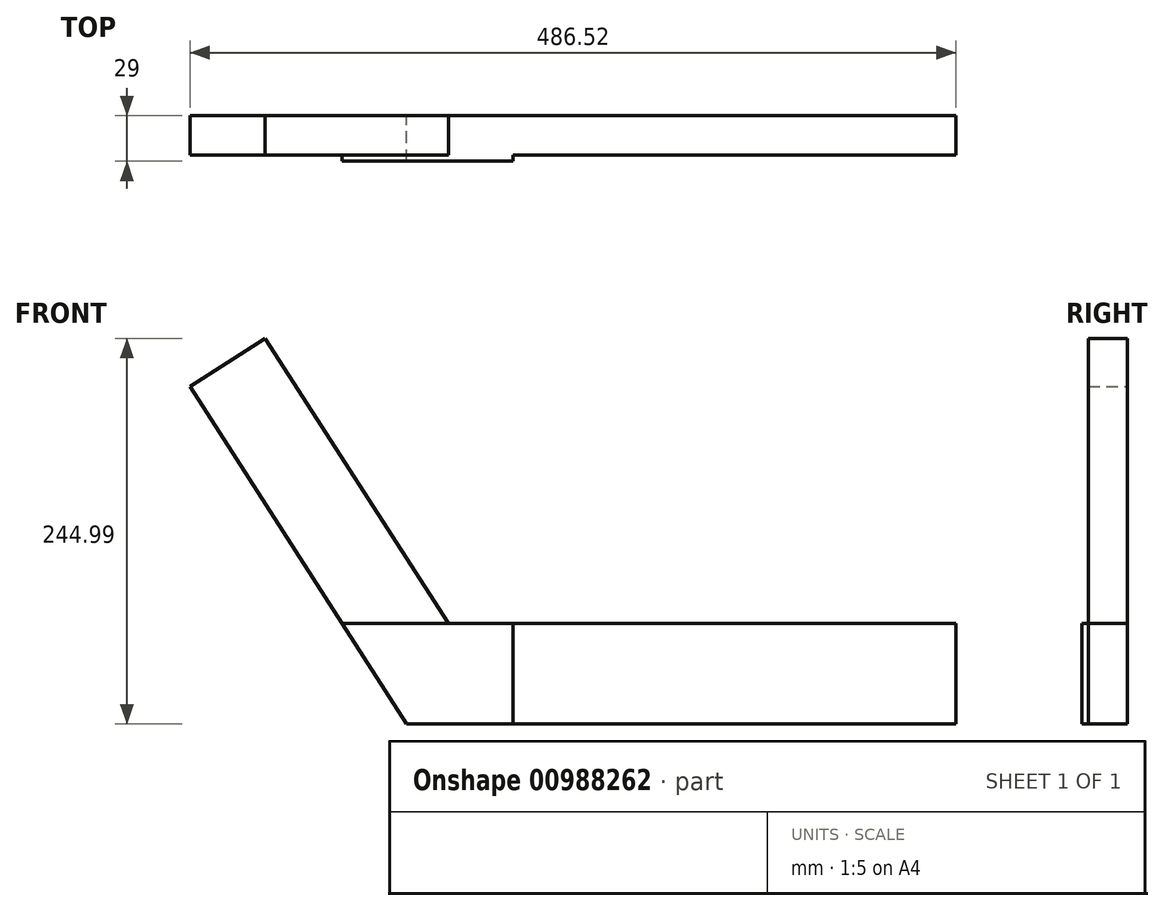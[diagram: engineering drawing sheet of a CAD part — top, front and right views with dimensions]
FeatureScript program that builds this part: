
annotation { "Feature Type Name" : "Feature", "Feature Type Description" : "" }
export const myFeature = defineFeature(function(context is Context, id is Id, definition is map)
    precondition{}
    {
        {
            var Q0;
            Q0=qCreatedBy(makeId("Front.planeOp"),FACE);
            var sketch = newSketch(context, id + "F0", { "sketchPlane" : qUnion([Q0])});
            skLineSegment(sketch, "E0", {"start": v(0, 0) * mm, "end": v(-157.46, 244.99) * mm});
            skLineSegment(sketch, "E1", {"start": v(-157.46, 244.99) * mm, "end": v(-205.3, 214.23) * mm});
            skLineSegment(sketch, "E2", {"start": v(-205.3, 214.23) * mm, "end": v(-67.62, 0) * mm});
            skLineSegment(sketch, "E3", {"start": v(-67.62, 0) * mm, "end": v(0, 0) * mm});
            skLineSegment(sketch, "E4", {"start": v(0, 0) * mm, "end": v(281.2, 0) * mm});
            skLineSegment(sketch, "E5", {"start": v(281.2, 0) * mm, "end": v(281.2, 63.89) * mm});
            skLineSegment(sketch, "E6", {"start": v(281.2, 63.89) * mm, "end": v(-41.06, 63.89) * mm});
            skLineSegment(sketch, "E7", {"start": v(-41.06, 63.89) * mm, "end": v(0, 0) * mm});
            skSolve(sketch);
        }
        {
            var Q0;
            Q0=makeQuery(id+"F0.imprint","IMPRINT",FACE,{"disambiguationData":[TD([[makeQuery(id+"F0.imprint","IMPRINT",EDGE,{"derivedFrom":sQuery(id+"F0.wireOp",EDGE,"E0")}),1.0]])]});
            extrude(context, id + "F1", {"entities" : qUnion([Q0]), "depth" : 25 * mm, "offsetDistance" : 25 * mm});
        }
        {
            var Q0;
            Q0=makeQuery(id+"F0.imprint","IMPRINT",FACE,{"disambiguationData":[TD([[makeQuery(id+"F0.imprint","IMPRINT",EDGE,{"derivedFrom":sQuery(id+"F0.wireOp",EDGE,"E4")}),1.0]])]});
            extrude(context, id + "F2", {"entities" : qUnion([Q0]), "operationType" : NewBodyOperationType.ADD, "depth" : 25 * mm, "offsetDistance" : 25 * mm});
        }
        {
            var Q0;
            {var subQ0=sQuery(id+"F0.wireOp",EDGE,"E7");Q0=makeQuery(id+"F2.boolean.opBoolean","MERGE",FACE,{"derivedFrom":[makeQuery(id+"F1.opExtrude","CAP_FACE",FACE,{"disambiguationData":[OSD([sQuery(id+"F0.wireOp",EDGE,"E0"),sQuery(id+"F0.wireOp",EDGE,"E1"),sQuery(id+"F0.wireOp",EDGE,"E2"),sQuery(id+"F0.wireOp",EDGE,"E3"),subQ0])],"isStart":false}),makeQuery(id+"F2.opExtrude","CAP_FACE",FACE,{"disambiguationData":[OSD([sQuery(id+"F0.wireOp",EDGE,"E4"),sQuery(id+"F0.wireOp",EDGE,"E5"),sQuery(id+"F0.wireOp",EDGE,"E6"),subQ0])],"isStart":false})]});}
            cPlane(context, id + "F3", {"entities" : qUnion([Q0]), "cplaneType" : CPlaneType.OFFSET, "offset" : 0 * mm, "width" : 150 * mm, "height" : 150 * mm});
        }
        {
            var Q0;
            Q0=qCreatedBy(id+"F3.planeOp",FACE);
            var sketch = newSketch(context, id + "F4", { "sketchPlane" : qUnion([Q0])});
            skLineSegment(sketch, "E8", {"start": v(0, 63.89) * mm, "end": v(-108.68, 63.89) * mm});
            skLineSegment(sketch, "E9", {"start": v(-108.68, 63.89) * mm, "end": v(-67.62, 0) * mm});
            skLineSegment(sketch, "E10", {"start": v(-67.62, 0) * mm, "end": v(0, 0) * mm});
            skLineSegment(sketch, "E11", {"start": v(0, 0) * mm, "end": v(0, 63.89) * mm});
            skSolve(sketch);
        }
        {
            var Q0;
            Q0=makeQuery(id+"F4.imprint","IMPRINT",FACE,{"disambiguationData":[TD([[makeQuery(id+"F4.imprint","IMPRINT",EDGE,{"derivedFrom":sQuery(id+"F4.wireOp",EDGE,"E8")}),1.0]])]});
            extrude(context, id + "F5", {"entities" : qUnion([Q0]), "operationType" : NewBodyOperationType.ADD, "depth" : 4 * mm, "offsetDistance" : 25 * mm});
        }
    });
